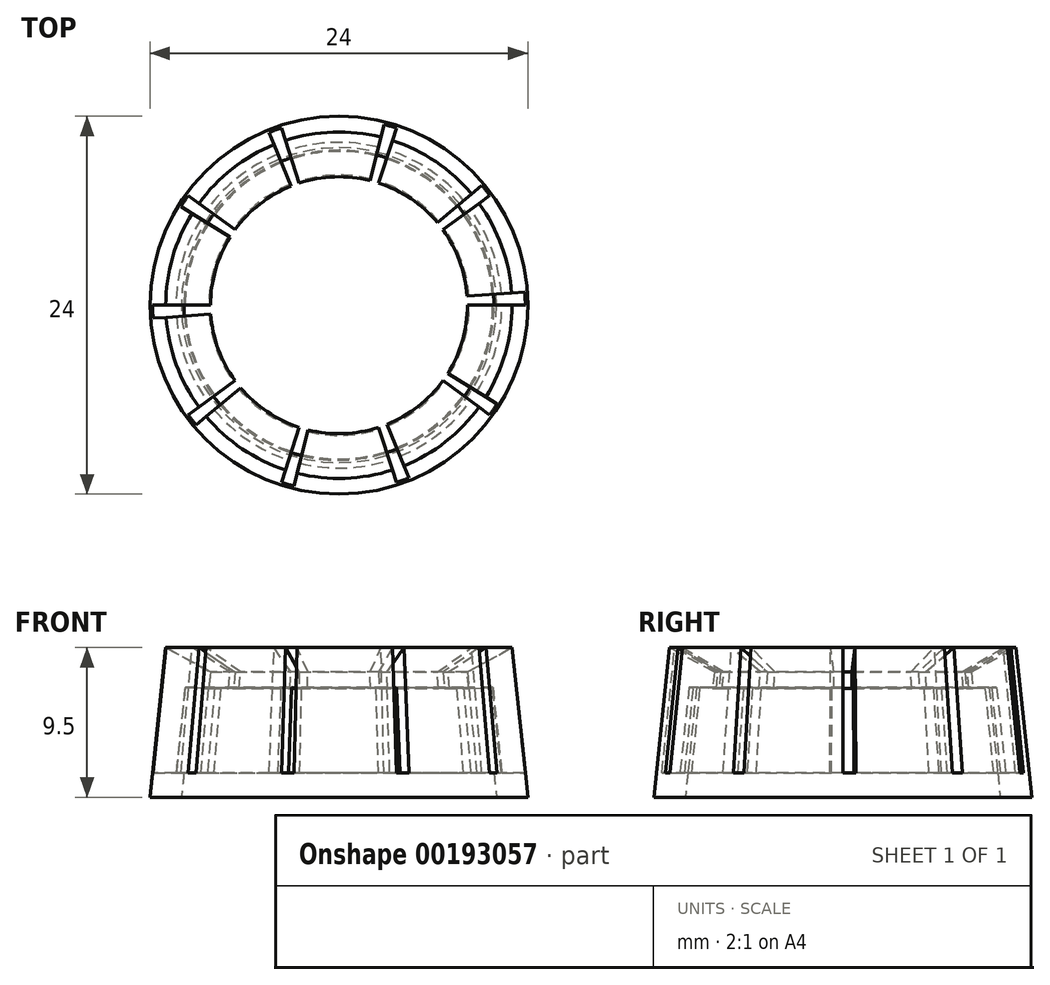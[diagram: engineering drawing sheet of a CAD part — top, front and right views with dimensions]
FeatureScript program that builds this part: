
annotation { "Feature Type Name" : "Feature", "Feature Type Description" : "" }
export const myFeature = defineFeature(function(context is Context, id is Id, definition is map)
    precondition{}
    {
        {
            var Q0;
            Q0=qCreatedBy(makeId("Front.planeOp"),FACE);
            var sketch = newSketch(context, id + "F0", { "sketchPlane" : qUnion([Q0])});
            skLineSegment(sketch, "E0.bottom", {"start": v(0, 0) * mm, "end": v(12, 0) * mm, "construction": true});
            skLineSegment(sketch, "E0.left", {"start": v(0, 0) * mm, "end": v(0, 9.5) * mm, "construction": true});
            skLineSegment(sketch, "E1", {"start": v(12, 0) * mm, "end": v(11, 9.5) * mm});
            skLineSegment(sketch, "E2.left", {"start": v(0, 0) * mm, "end": v(0, 1.5) * mm, "construction": true});
            skLineSegment(sketch, "E3.bottom", {"start": v(0, 0) * mm, "end": v(12, 0) * mm});
            skLineSegment(sketch, "E3.left", {"start": v(0, 0) * mm, "end": v(0, 7) * mm});
            skLineSegment(sketch, "E4.0", {"start": v(10, 0) * mm, "end": v(9.85, 1.5) * mm});
            skLineSegment(sketch, "E5.0", {"start": v(10.35, 1.47) * mm, "end": v(9.77, 6.97) * mm});
            skLineSegment(sketch, "E6.0", {"start": v(8.27, 6.9) * mm, "end": v(8.16, 7.94) * mm});
            skLineSegment(sketch, "E7", {"start": v(10.34, 1.55) * mm, "end": v(9.84, 1.55) * mm});
            skLineSegment(sketch, "E8", {"start": v(9.84, 1.55) * mm, "end": v(9.85, 1.5) * mm});
            skLineSegment(sketch, "E9", {"start": v(9.77, 6.97) * mm, "end": v(9.77, 7) * mm});
            skLineSegment(sketch, "E10", {"start": v(9.77, 6.97) * mm, "end": v(8.27, 6.9) * mm});
            skLineSegment(sketch, "E11", {"start": v(11, 9.5) * mm, "end": v(8.16, 7.94) * mm});
            skPoint(sketch, "E12.0.start.orphan", {"position": v(10.5, 0) * mm});
            skSolve(sketch);
        }
        {
            var Q0;
            {var subQ2=sQuery(id+"F0.wireOp",EDGE,"E1");Q0=makeQuery(id+"F0.imprint","IMPRINT",FACE,{"disambiguationData":[TD([[makeQuery(id+"F0.imprint","IMPRINT",EDGE,{"derivedFrom":subQ2}),1.0]])]});}
            var Q1;
            Q1=sQuery(id+"F0.wireOp",EDGE,"E3.left");
            revolve(context, id + "F1", {"entities" : qUnion([Q0]), "axis" : qUnion([Q1]), "revolveType" : RevolveType.FULL});
        }
        {
            var Q0;
            Q0=makeQuery(id+"F1.opRevolve","SWEPT_FACE",FACE,{"disambiguationData":[OSD([sQuery(id+"F0.wireOp",EDGE,"E7")])]});
            var sketch = newSketch(context, id + "F2", { "sketchPlane" : qUnion([Q0])});
            skLineSegment(sketch, "E13", {"start": v(0, 0) * mm, "end": v(-13.19, 0) * mm});
            skLineSegment(sketch, "E14", {"start": v(-13.19, -0.92) * mm, "end": v(-13.19, 0) * mm});
            skLineSegment(sketch, "E15", {"start": v(-13.19, -0.92) * mm, "end": v(0, 0) * mm});
            skLineSegment(sketch, "E16.1.0", {"start": v(-10.13, -8.5) * mm, "end": v(0, 0) * mm});
            skLineSegment(sketch, "E16.1.1", {"start": v(-10.13, -8.5) * mm, "end": v(-10.67, -7.75) * mm});
            skLineSegment(sketch, "E16.1.2", {"start": v(0, 0) * mm, "end": v(-10.67, -7.75) * mm});
            skLineSegment(sketch, "E16.2.0", {"start": v(-3.2, -12.83) * mm, "end": v(0, 0) * mm});
            skLineSegment(sketch, "E16.2.1", {"start": v(-3.2, -12.83) * mm, "end": v(-4.08, -12.54) * mm});
            skLineSegment(sketch, "E16.2.2", {"start": v(0, 0) * mm, "end": v(-4.08, -12.54) * mm});
            skLineSegment(sketch, "E16.3.0", {"start": v(4.95, -12.26) * mm, "end": v(0, 0) * mm});
            skLineSegment(sketch, "E16.3.1", {"start": v(4.95, -12.26) * mm, "end": v(4.08, -12.54) * mm});
            skLineSegment(sketch, "E16.3.2", {"start": v(0, 0) * mm, "end": v(4.08, -12.54) * mm});
            skLineSegment(sketch, "E16.4.0", {"start": v(11.21, -7) * mm, "end": v(0, 0) * mm});
            skLineSegment(sketch, "E16.4.1", {"start": v(11.21, -7) * mm, "end": v(10.67, -7.75) * mm});
            skLineSegment(sketch, "E16.4.2", {"start": v(0, 0) * mm, "end": v(10.67, -7.75) * mm});
            skLineSegment(sketch, "E16.5.0", {"start": v(13.19, 0.92) * mm, "end": v(0, 0) * mm});
            skLineSegment(sketch, "E16.5.1", {"start": v(13.19, 0.92) * mm, "end": v(13.19, 0) * mm});
            skLineSegment(sketch, "E16.5.2", {"start": v(0, 0) * mm, "end": v(13.19, 0) * mm});
            skLineSegment(sketch, "E16.6.0", {"start": v(10.13, 8.5) * mm, "end": v(0, 0) * mm});
            skLineSegment(sketch, "E16.6.1", {"start": v(10.13, 8.5) * mm, "end": v(10.67, 7.75) * mm});
            skLineSegment(sketch, "E16.6.2", {"start": v(0, 0) * mm, "end": v(10.67, 7.75) * mm});
            skLineSegment(sketch, "E16.7.0", {"start": v(3.2, 12.83) * mm, "end": v(0, 0) * mm});
            skLineSegment(sketch, "E16.7.1", {"start": v(3.2, 12.83) * mm, "end": v(4.08, 12.54) * mm});
            skLineSegment(sketch, "E16.7.2", {"start": v(0, 0) * mm, "end": v(4.08, 12.54) * mm});
            skLineSegment(sketch, "E16.8.0", {"start": v(-4.95, 12.26) * mm, "end": v(0, 0) * mm});
            skLineSegment(sketch, "E16.8.1", {"start": v(-4.95, 12.26) * mm, "end": v(-4.08, 12.54) * mm});
            skLineSegment(sketch, "E16.8.2", {"start": v(0, 0) * mm, "end": v(-4.08, 12.54) * mm});
            skLineSegment(sketch, "E16.9.0", {"start": v(-11.21, 7) * mm, "end": v(0, 0) * mm});
            skLineSegment(sketch, "E16.9.1", {"start": v(-11.21, 7) * mm, "end": v(-10.67, 7.75) * mm});
            skLineSegment(sketch, "E16.9.2", {"start": v(0, 0) * mm, "end": v(-10.67, 7.75) * mm});
            skPoint(sketch, "E16.center", {"position": v(0, 0) * mm});
            skSolve(sketch);
        }
        {
            var Q0;
            Q0 = qSketchRegion(id + "F2", true);
            extrude(context, id + "F3", {"entities" : qUnion([Q0]), "operationType" : NewBodyOperationType.REMOVE, "depth" : 25 * mm});
        }
    });
